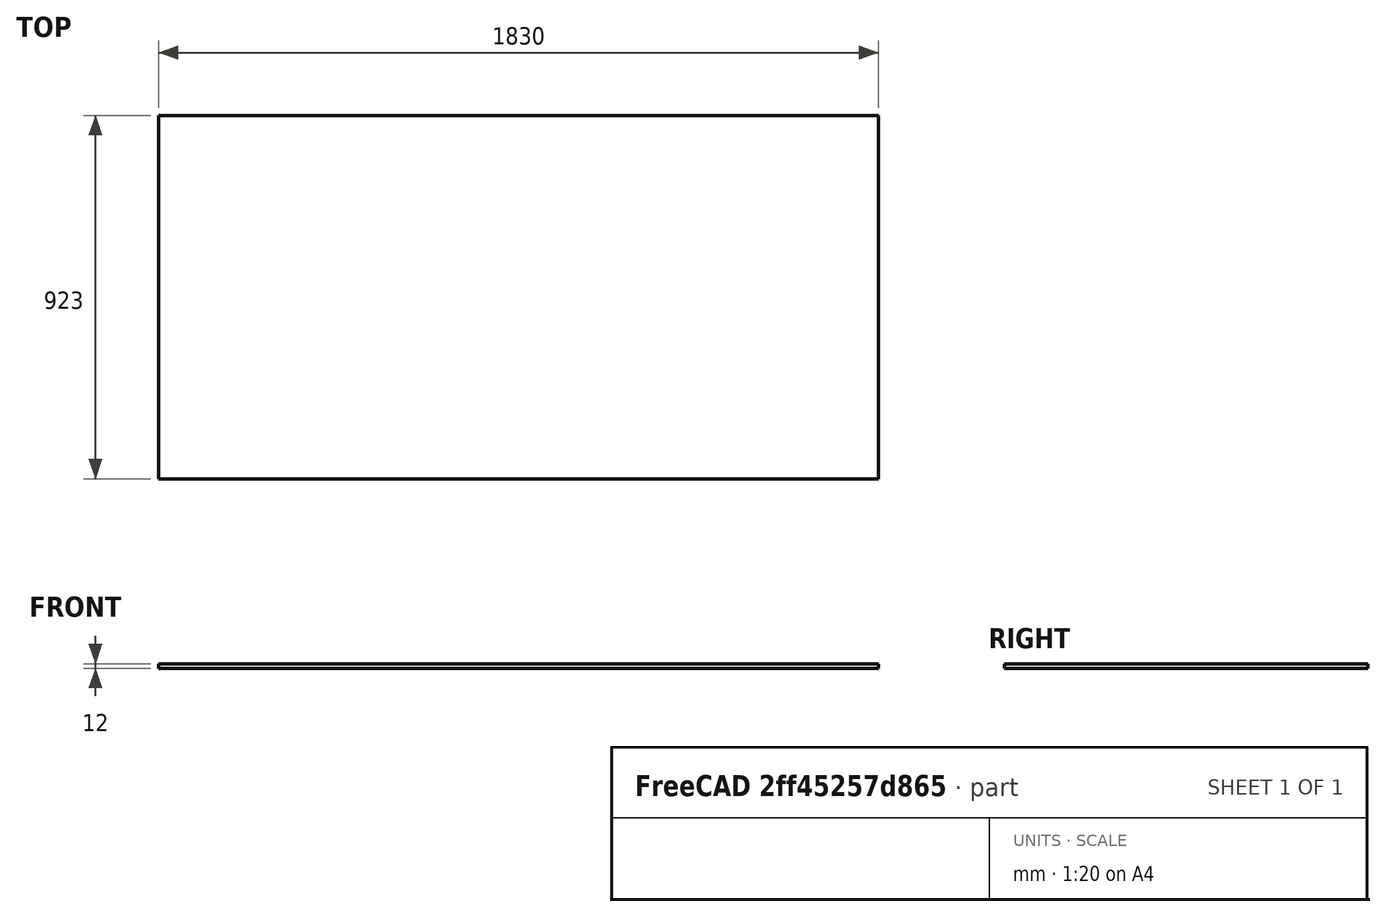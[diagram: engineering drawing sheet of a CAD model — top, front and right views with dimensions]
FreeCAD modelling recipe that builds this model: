
FCSTD DOCUMENT  (FreeCAD 0.17R7761 (Git))
Label: 6X3_workspace
License: CreativeCommons Attribution-ShareAlike
LicenseURL: http://creativecommons.org/licenses/by-sa/4.0/
objects: Sketcher::SketchObject×1, PartDesign::Pad×1, PartDesign::Body×1
note: 4 computed .brp shape members not serialized (recipe doc carries the construction recipe); baked Part::Feature solids carry a one-line shape summary decoded from their .brp

FEATURE [Sketcher::SketchObject] Sketch
  MapMode = 5
  Support = -> [XY_Plane]
  sketch-geometry (4):
    g0: LineSegment StartX=-843.552 StartY=-527.039 StartZ=0 EndX=986.448 EndY=-527.039 EndZ=0
    g1: LineSegment StartX=986.448 StartY=-527.039 StartZ=0 EndX=986.448 EndY=395.961 EndZ=0
    g2: LineSegment StartX=986.448 StartY=395.961 StartZ=0 EndX=-843.552 EndY=395.961 EndZ=0
    g3: LineSegment StartX=-843.552 StartY=395.961 StartZ=0 EndX=-843.552 EndY=-527.039 EndZ=0
  constraints (10):
    c: Coincident(g0,g1)
    c: Coincident(g1,g2)
    c: Coincident(g2,g3)
    c: Coincident(g3,g0)
    c: Horizontal(g0)
    c: Horizontal(g2)
    c: Vertical(g1)
    c: Vertical(g3)
    c: DistanceX(g2,g2) = 1830
    c: DistanceY(g3,g3) = 923
FEATURE [PartDesign::Pad] Pad
  Length = 12
  Length2 = 100
  Profile = -> Sketch
  Type = 0
FEATURE [PartDesign::Body] Body
  Model = -> [Sketch,Pad]
  Origin = -> BodyOrigin
  Tip = -> Pad
